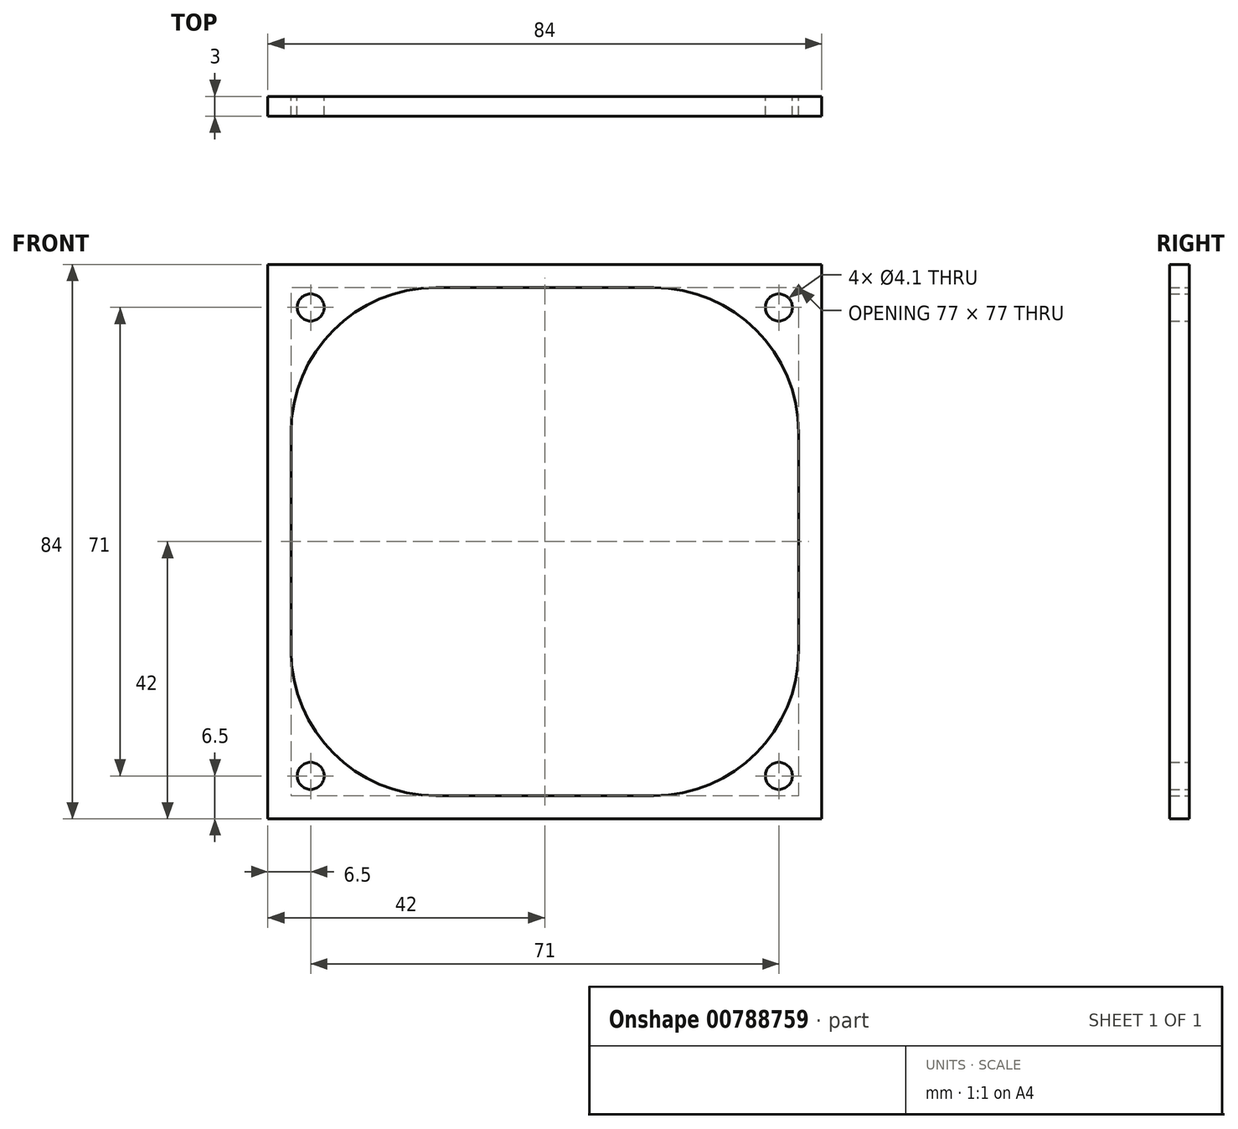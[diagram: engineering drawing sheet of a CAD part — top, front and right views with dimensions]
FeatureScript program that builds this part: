
annotation { "Feature Type Name" : "Feature", "Feature Type Description" : "" }
export const myFeature = defineFeature(function(context is Context, id is Id, definition is map)
    precondition{}
    {
        {
            var Q0;
            Q0=qCreatedBy(makeId("Front.planeOp"),FACE);
            var sketch = newSketch(context, id + "F0", { "sketchPlane" : qUnion([Q0])});
            skLineSegment(sketch, "E0.bottom", {"start": v(42, 42) * mm, "end": v(-42, 42) * mm});
            skLineSegment(sketch, "E0.top", {"start": v(42, -42) * mm, "end": v(-42, -42) * mm});
            skLineSegment(sketch, "E0.left", {"start": v(42, 42) * mm, "end": v(42, -42) * mm});
            skLineSegment(sketch, "E0.right", {"start": v(-42, 42) * mm, "end": v(-42, -42) * mm});
            skPoint(sketch, "E0.middle", {"position": v(0, 0) * mm});
            skLineSegment(sketch, "E1.bottom", {"start": v(16.5, 38.5) * mm, "end": v(-16.5, 38.5) * mm});
            skLineSegment(sketch, "E1.top", {"start": v(16.5, -38.5) * mm, "end": v(-16.5, -38.5) * mm});
            skLineSegment(sketch, "E1.left", {"start": v(38.5, 16.5) * mm, "end": v(38.5, -16.5) * mm});
            skLineSegment(sketch, "E1.right", {"start": v(-38.5, 16.5) * mm, "end": v(-38.5, -16.5) * mm});
            skArc(sketch, "E2.filletArc", {"start": v(38.5, 16.5) * mm, "mid": v(32.06, 32.06) * mm, "end": v(16.5, 38.5) * mm});
            skArc(sketch, "E3.filletArc", {"start": v(-16.5, 38.5) * mm, "mid": v(-32.06, 32.06) * mm, "end": v(-38.5, 16.5) * mm});
            skArc(sketch, "E4.filletArc", {"start": v(-38.5, -16.5) * mm, "mid": v(-32.06, -32.06) * mm, "end": v(-16.5, -38.5) * mm});
            skArc(sketch, "E5.filletArc", {"start": v(16.5, -38.5) * mm, "mid": v(32.06, -32.06) * mm, "end": v(38.5, -16.5) * mm});
            skLineSegment(sketch, "E6", {"start": v(16.5, -38.5) * mm, "end": v(16.5, 38.5) * mm, "construction": true});
            skLineSegment(sketch, "E7.bottom", {"start": v(35.5, 35.5) * mm, "end": v(-35.5, 35.5) * mm, "construction": true});
            skLineSegment(sketch, "E7.top", {"start": v(35.5, -35.5) * mm, "end": v(-35.5, -35.5) * mm, "construction": true});
            skLineSegment(sketch, "E7.left", {"start": v(35.5, 35.5) * mm, "end": v(35.5, -35.5) * mm, "construction": true});
            skLineSegment(sketch, "E7.right", {"start": v(-35.5, 35.5) * mm, "end": v(-35.5, -35.5) * mm, "construction": true});
            skCircle(sketch, "E8", {"center": v(-35.5, 35.5) * mm, "radius": 2.05 * mm});
            skCircle(sketch, "E9.MirrorC", {"center": v(35.5, 35.5) * mm, "radius": 2.05 * mm});
            skCircle(sketch, "E10.MirrorC", {"center": v(35.5, -35.5) * mm, "radius": 2.05 * mm});
            skCircle(sketch, "E11.MirrorC", {"center": v(-35.5, -35.5) * mm, "radius": 2.05 * mm});
            skLineSegment(sketch, "E12.bottom", {"start": v(39.5, 39.5) * mm, "end": v(-39.5, 39.5) * mm});
            skLineSegment(sketch, "E12.top", {"start": v(39.5, -39.5) * mm, "end": v(-39.5, -39.5) * mm});
            skLineSegment(sketch, "E12.left", {"start": v(39.5, 39.5) * mm, "end": v(39.5, -39.5) * mm});
            skLineSegment(sketch, "E12.right", {"start": v(-39.5, 39.5) * mm, "end": v(-39.5, -39.5) * mm});
            skLineSegment(sketch, "E13", {"start": v(-42, 0) * mm, "end": v(42, 0) * mm, "construction": true});
            skLineSegment(sketch, "E14", {"start": v(0, 42) * mm, "end": v(0, -42) * mm, "construction": true});
            skSolve(sketch);
        }
        {
            var Q0;
            Q0=makeQuery(id+"F0.imprint","IMPRINT",FACE,{"disambiguationData":[TD([[makeQuery(id+"F0.imprint","IMPRINT",EDGE,{"derivedFrom":sQuery(id+"F0.wireOp",EDGE,"E1.bottom")}),-1.0]])]});
            var Q1;
            Q1=makeQuery(id+"F0.imprint","IMPRINT",FACE,{"disambiguationData":[TD([[makeQuery(id+"F0.imprint","IMPRINT",EDGE,{"derivedFrom":sQuery(id+"F0.wireOp",EDGE,"E0.bottom")}),1.0]])]});
            extrude(context, id + "F1", {"entities" : qUnion([Q0, Q1]), "depth" : 3 * mm, "offsetDistance" : 25 * mm});
        }
    });
